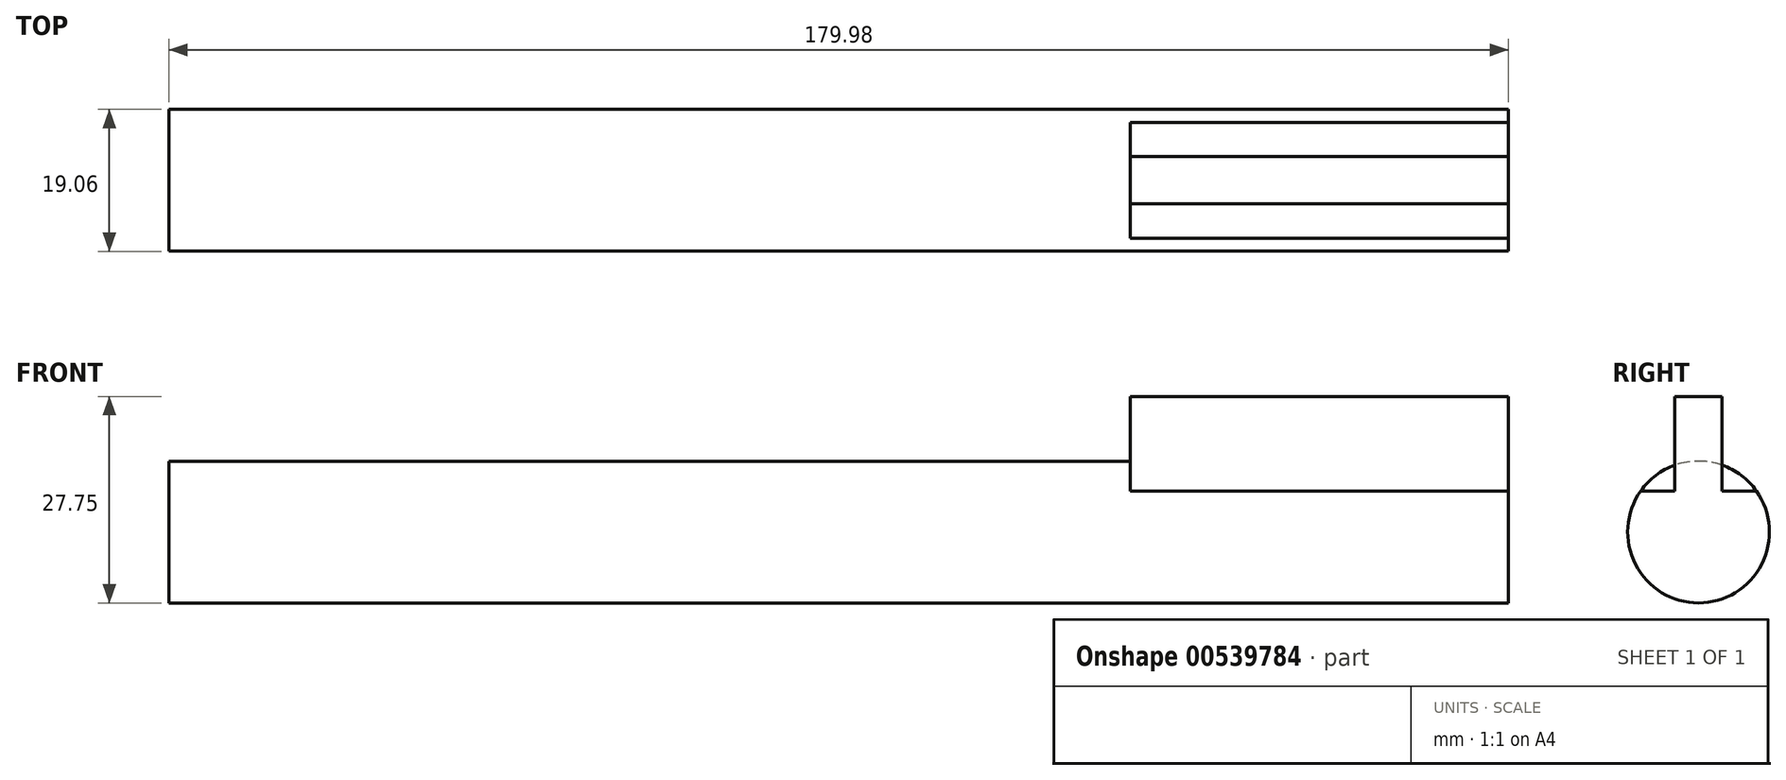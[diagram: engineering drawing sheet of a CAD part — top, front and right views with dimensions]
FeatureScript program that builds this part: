
annotation { "Feature Type Name" : "Feature", "Feature Type Description" : "" }
export const myFeature = defineFeature(function(context is Context, id is Id, definition is map)
    precondition{}
    {
        {
            var Q0;
            Q0=qCreatedBy(makeId("Right.planeOp"),FACE);
            var sketch = newSketch(context, id + "F0", { "sketchPlane" : qUnion([Q0])});
            skCircle(sketch, "E0", {"center": v(0, 0) * mm, "radius": 9.53 * mm});
            skSolve(sketch);
        }
        {
            var Q0;
            Q0=makeQuery(id+"F0.imprint","IMPRINT",FACE,{"disambiguationData":[TD([[makeQuery(id+"F0.imprint","IMPRINT",EDGE,{"derivedFrom":sQuery(id+"F0.wireOp",EDGE,"E0")}),1.0]])]});
            extrude(context, id + "F1", {"entities" : qUnion([Q0]), "oppositeDirection" : true, "depth" : 179.98 * mm, "offsetDistance" : 25.4 * mm});
        }
        {
            var Q0;
            Q0=makeQuery(id+"F1.opExtrude","CAP_FACE",FACE,{"disambiguationData":[OSD([sQuery(id+"F0.wireOp",EDGE,"E0")])],"isStart":true});
            var sketch = newSketch(context, id + "F2", { "sketchPlane" : qUnion([Q0])});
            skLineSegment(sketch, "E1", {"start": v(0, 5.52) * mm, "end": v(7.76, 5.52) * mm});
            skLineSegment(sketch, "E2", {"start": v(0, 5.52) * mm, "end": v(-7.76, 5.52) * mm});
            skArc(sketch, "E3", {"start": v(7.76, 5.52) * mm, "mid": v(0, 9.53) * mm, "end": v(-7.76, 5.52) * mm});
            skSolve(sketch);
        }
        {
            var Q0;
            Q0=makeQuery(id+"F2.imprint","IMPRINT",FACE,{"disambiguationData":[TD([[makeQuery(id+"F2.imprint","IMPRINT",EDGE,{"derivedFrom":sQuery(id+"F2.wireOp",EDGE,"E1")}),1.0]])]});
            extrude(context, id + "F3", {"entities" : qUnion([Q0]), "operationType" : NewBodyOperationType.REMOVE, "oppositeDirection" : true, "depth" : 50.8 * mm, "offsetDistance" : 25.4 * mm});
        }
        {
            var Q0;
            Q0=makeQuery(id+"F3.boolean.opBoolean","COPY",FACE,{"derivedFrom":makeQuery(id+"F3.opExtrude","SWEPT_FACE",FACE,{"disambiguationData":[OSD([sQuery(id+"F2.wireOp",EDGE,"E1"),sQuery(id+"F2.wireOp",EDGE,"E2")])]})});
            var sketch = newSketch(context, id + "F4", { "sketchPlane" : qUnion([Q0])});
            skLineSegment(sketch, "E4.0", {"start": v(0, 3.18) * mm, "end": v(-50.8, 3.18) * mm});
            skLineSegment(sketch, "E5.0", {"start": v(0, -3.17) * mm, "end": v(-50.8, -3.17) * mm});
            skLineSegment(sketch, "E6", {"start": v(-50.8, 3.18) * mm, "end": v(-50.8, -3.17) * mm});
            skLineSegment(sketch, "E7", {"start": v(0, 3.18) * mm, "end": v(0, -3.17) * mm});
            skSolve(sketch);
        }
        {
            var Q0;
            Q0 = qSketchRegion(id + "F4", true);
            extrude(context, id + "F5", {"entities" : qUnion([Q0]), "operationType" : NewBodyOperationType.ADD, "depth" : 12.7 * mm, "offsetDistance" : 25.4 * mm});
        }
    });
